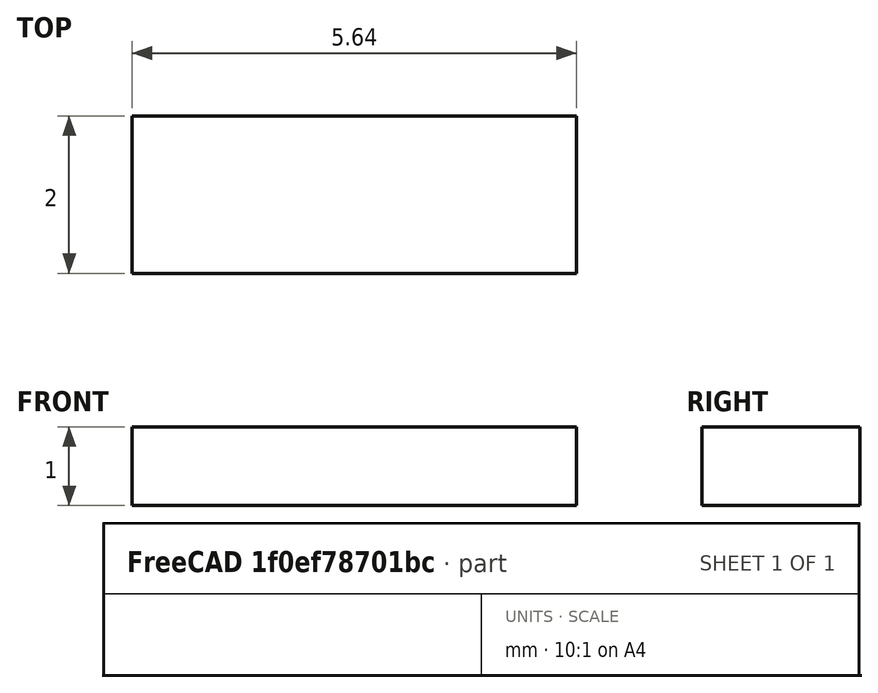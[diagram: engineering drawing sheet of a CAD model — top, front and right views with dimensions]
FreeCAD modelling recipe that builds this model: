
FCSTD DOCUMENT  (FreeCAD 1.0R39109 (Git))
Label: ANT
License: All rights reserved
objects: Sketcher::SketchObject×1, PartDesign::Pad×1, PartDesign::Body×1
note: 6 computed .brp shape members not serialized (recipe doc carries the construction recipe); baked Part::Feature solids carry a one-line shape summary decoded from their .brp

FEATURE [Sketcher::SketchObject] Sketch
  ArcFitTolerance = 1e-06
  AttachmentSupport = -> [XY_Plane]
  FullyConstrained = true
  MakeInternals = false
  MapMode = 5
  sketch-geometry (4):
    g0: LineSegment StartX=-2.82 StartY=1 StartZ=0 EndX=-2.82 EndY=-1 EndZ=0
    g1: LineSegment StartX=-2.82 StartY=-1 StartZ=0 EndX=2.82 EndY=-1 EndZ=0
    g2: LineSegment StartX=2.82 StartY=-1 StartZ=0 EndX=2.82 EndY=1 EndZ=0
    g3: LineSegment StartX=2.82 StartY=1 StartZ=0 EndX=-2.82 EndY=1 EndZ=0
  constraints (12):
    c: Coincident(g0,g1)
    c: Coincident(g1,g2)
    c: Coincident(g2,g3)
    c: Coincident(g3,g0)
    c: Vertical(g0)
    c: Vertical(g2)
    c: Horizontal(g1)
    c: Horizontal(g3)
    c: DistanceY(g0,g0) = 2
    c: DistanceX(g3,g3) = 5.64
    c: DistanceY(g0,g-1) = 1
    c: DistanceX(g0,g-1) = 2.82
FEATURE [PartDesign::Pad] Pad
  Direction = (0,0,1)
  Length = 1
  Length2 = 10
  Profile = -> Sketch
  ReferenceAxis = -> Sketch [N_Axis]
  Refine = true
  Suppressed = false
  Type = 0
FEATURE [PartDesign::Body] Body
  AllowCompound = false
  Group = -> [Sketch,Pad]
  Origin = -> Origin
  Tip = -> Pad
